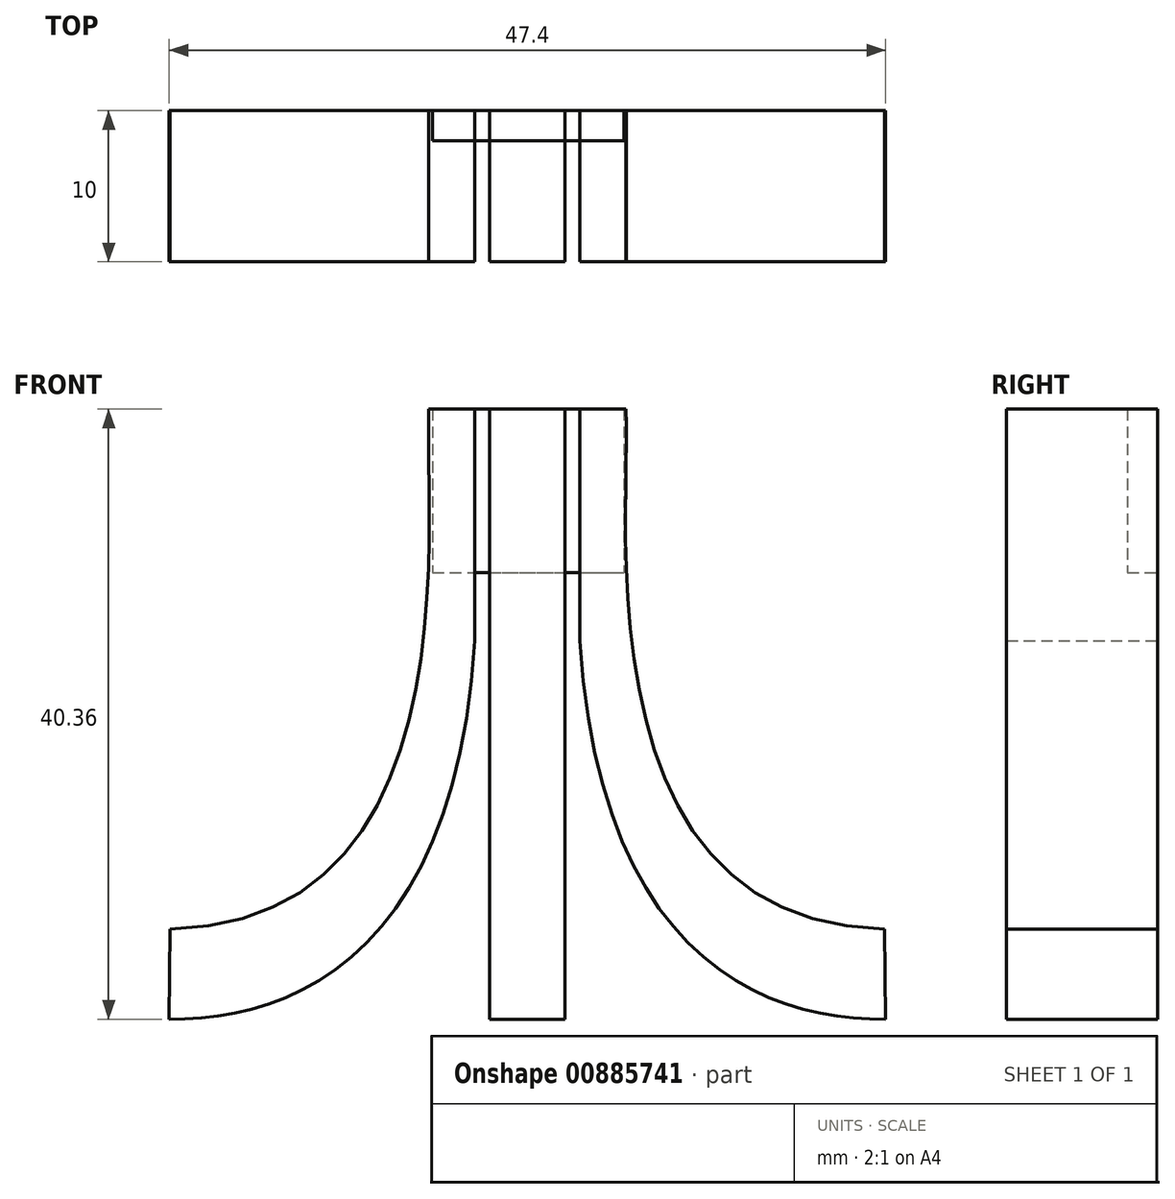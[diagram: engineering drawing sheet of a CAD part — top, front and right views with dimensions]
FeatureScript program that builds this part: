
annotation { "Feature Type Name" : "Feature", "Feature Type Description" : "" }
export const myFeature = defineFeature(function(context is Context, id is Id, definition is map)
    precondition{}
    {
        {
            var Q0;
            Q0=qCreatedBy(makeId("Front.planeOp"),FACE);
            var sketch = newSketch(context, id + "F0", { "sketchPlane" : qUnion([Q0])});
            skLineSegment(sketch, "E0", {"start": v(0, 61.48) * mm, "end": v(0, 0) * mm, "construction": true});
            skLineSegment(sketch, "E1", {"start": v(24.8, 21.12) * mm, "end": v(-24.8, 21.12) * mm, "construction": true});
            skSolve(sketch);
        }
        {
            var Q0;
            Q0=qCreatedBy(makeId("Front.planeOp"),FACE);
            var sketch = newSketch(context, id + "F1", { "sketchPlane" : qUnion([Q0])});
            skLineSegment(sketch, "E2", {"start": v(-6.52, 61.48) * mm, "end": v(-3.47, 61.48) * mm});
            skLineSegment(sketch, "E3", {"start": v(-23.64, 27.1) * mm, "end": v(-23.7, 21.12) * mm});
            skLineSegment(sketch, "E4", {"start": v(-3.47, 61.48) * mm, "end": v(-3.47, 46.14) * mm});
            skFitSpline(sketch, "E5", {"points": [v(-3.47, 46.14) * mm, v(-23.7, 21.12) * mm], "startDerivative": vector(-4.06, -63.24) * mm, "endDerivative": vector(-23.69, 0.25) * mm});
            skFitSpline(sketch, "E6", {"points": [v(-6.52, 61.48) * mm, v(-23.64, 27.1) * mm], "startDerivative": vector(-1.12, -20.28) * mm, "endDerivative": vector(-60.96, -1.32) * mm});
            skLineSegment(sketch, "E7", {"start": v(0, 61.48) * mm, "end": v(-2.49, 61.48) * mm});
            skLineSegment(sketch, "E8", {"start": v(-2.49, 61.48) * mm, "end": v(-2.49, 21.12) * mm});
            skLineSegment(sketch, "E9", {"start": v(-2.49, 21.12) * mm, "end": v(0, 21.12) * mm});
            skLineSegment(sketch, "E10.MirrorCS", {"start": v(0, 61.48) * mm, "end": v(2.49, 61.48) * mm});
            skLineSegment(sketch, "E11.MirrorCS", {"start": v(2.49, 61.48) * mm, "end": v(2.49, 21.12) * mm});
            skLineSegment(sketch, "E12.MirrorCS", {"start": v(2.49, 21.12) * mm, "end": v(0, 21.12) * mm});
            skLineSegment(sketch, "E13.MirrorCS", {"start": v(3.47, 61.48) * mm, "end": v(3.47, 46.14) * mm});
            skFitSpline(sketch, "E14.MirrorCS", {"points": [v(3.47, 46.14) * mm, v(23.7, 21.12) * mm], "startDerivative": vector(4.06, -63.24) * mm, "endDerivative": vector(23.69, 0.25) * mm});
            skFitSpline(sketch, "E15.MirrorCS", {"points": [v(6.52, 61.48) * mm, v(23.64, 27.1) * mm], "startDerivative": vector(1.12, -20.28) * mm, "endDerivative": vector(60.96, -1.32) * mm});
            skLineSegment(sketch, "E16.MirrorCS", {"start": v(6.52, 61.48) * mm, "end": v(3.47, 61.48) * mm});
            skLineSegment(sketch, "E17.MirrorCS", {"start": v(23.64, 27.1) * mm, "end": v(23.7, 21.12) * mm});
            skSolve(sketch);
        }
        {
            var Q0;
            Q0 = qSketchRegion(id + "F1", true);
            extrude(context, id + "F2", {"entities" : qUnion([Q0]), "depth" : 10 * mm, "offsetDistance" : 25 * mm});
        }
        {
            var Q0;
            Q0=qCreatedBy(makeId("Front.planeOp"),FACE);
            var sketch = newSketch(context, id + "F3", { "sketchPlane" : qUnion([Q0])});
            skLineSegment(sketch, "E18.bottom", {"start": v(-6.28, 61.48) * mm, "end": v(6.37, 61.48) * mm});
            skLineSegment(sketch, "E18.top", {"start": v(-6.28, 50.66) * mm, "end": v(6.37, 50.66) * mm});
            skLineSegment(sketch, "E18.left", {"start": v(-6.28, 61.48) * mm, "end": v(-6.28, 50.66) * mm});
            skLineSegment(sketch, "E18.right", {"start": v(6.37, 61.48) * mm, "end": v(6.37, 50.66) * mm});
            skSolve(sketch);
        }
        {
            var Q0;
            Q0 = qSketchRegion(id + "F3", true);
            extrude(context, id + "F4", {"entities" : qUnion([Q0]), "depth" : 2 * mm, "offsetDistance" : 25 * mm});
        }
    });
